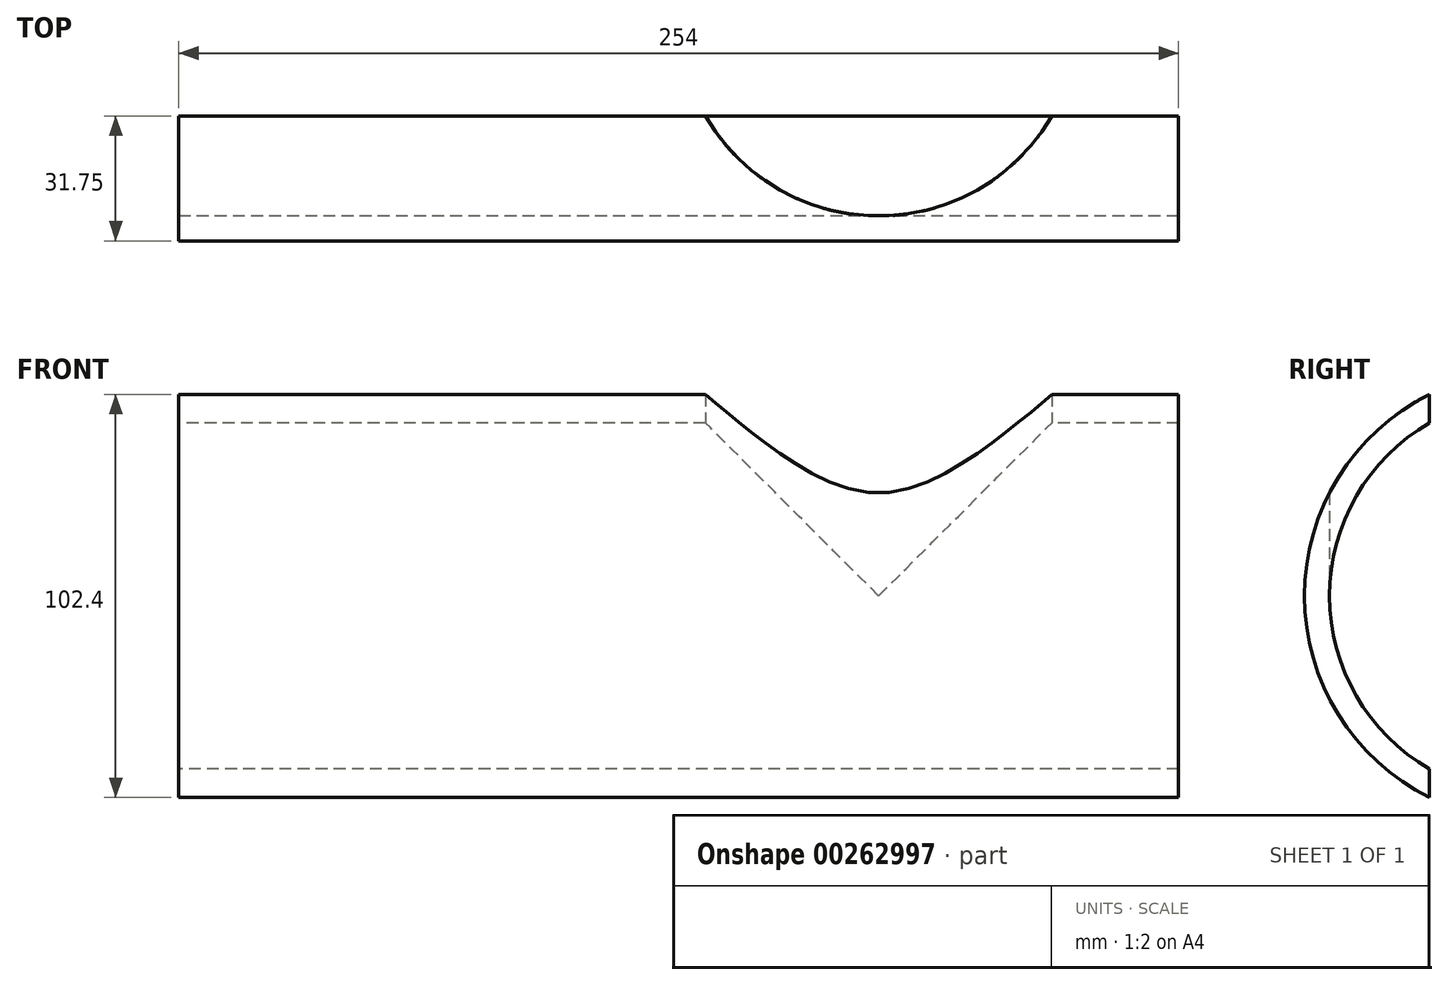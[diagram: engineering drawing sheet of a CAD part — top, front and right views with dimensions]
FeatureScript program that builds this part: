
annotation { "Feature Type Name" : "Feature", "Feature Type Description" : "" }
export const myFeature = defineFeature(function(context is Context, id is Id, definition is map)
    precondition{}
    {
        {
            var Q0;
            Q0=qCreatedBy(makeId("Right.planeOp"),FACE);
            var sketch = newSketch(context, id + "F0", { "sketchPlane" : qUnion([Q0])});
            skCircle(sketch, "E0", {"center": v(0, 0) * mm, "radius": 57.15 * mm});
            skCircle(sketch, "E1", {"center": v(0, 0) * mm, "radius": 50.8 * mm});
            skLineSegment(sketch, "E2", {"start": v(-25.4, 51.2) * mm, "end": v(-25.4, -51.2) * mm});
            skSolve(sketch);
        }
        {
            var Q0;
            {var subQ0=sQuery(id+"F0.wireOp",EDGE,"E2");var subQ1=sQuery(id+"F0.wireOp",EDGE,"E0");var subQ2=makeQuery(id+"F0.imprint","INTERSECT",VERTEX,{"disambiguationData":[OD(0.0)],"derivedFrom":[subQ1,subQ0]});Q0=makeQuery(id+"F0.imprint","IMPRINT",FACE,{"disambiguationData":[TD([[makeQuery(id+"F0.imprint","IMPRINT",EDGE,{"disambiguationData":[TD([[subQ2,1.0]])],"derivedFrom":subQ1}),1.0]])]});}
            extrude(context, id + "F1", {"entities" : qUnion([Q0]), "depth" : 254 * mm});
        }
        {
            var Q0;
            Q0=qCreatedBy(makeId("Top.planeOp"),FACE);
            var sketch = newSketch(context, id + "F2", { "sketchPlane" : qUnion([Q0])});
            skCircle(sketch, "E3", {"center": v(177.8, 0) * mm, "radius": 50.8 * mm});
            skSolve(sketch);
        }
        {
            var Q0;
            Q0=makeQuery(id+"F2.imprint","IMPRINT",FACE,{"disambiguationData":[TD([[makeQuery(id+"F2.imprint","IMPRINT",EDGE,{"derivedFrom":sQuery(id+"F2.wireOp",EDGE,"E3")}),1.0]])]});
            extrude(context, id + "F3", {"entities" : qUnion([Q0]), "operationType" : NewBodyOperationType.REMOVE, "depth" : 148.34 * mm});
        }
        {
            var Q0;
            Q0=qCreatedBy(makeId("Front.planeOp"),FACE);
            var sketch = newSketch(context, id + "F4", { "sketchPlane" : qUnion([Q0])});
            skCircle(sketch, "E4", {"center": v(127, -37.64) * mm, "radius": 3.54 * mm});
            skSolve(sketch);
        }
        {
            var Q0;
            Q0=makeQuery(id+"F4.imprint","IMPRINT",FACE,{"disambiguationData":[TD([[makeQuery(id+"F4.imprint","IMPRINT",EDGE,{"derivedFrom":sQuery(id+"F4.wireOp",EDGE,"E4")}),1.0]])]});
            extrude(context, id + "F5", {"entities" : qUnion([Q0]), "operationType" : NewBodyOperationType.REMOVE, "oppositeDirection" : true, "depth" : 89.92 * mm});
        }
    });
